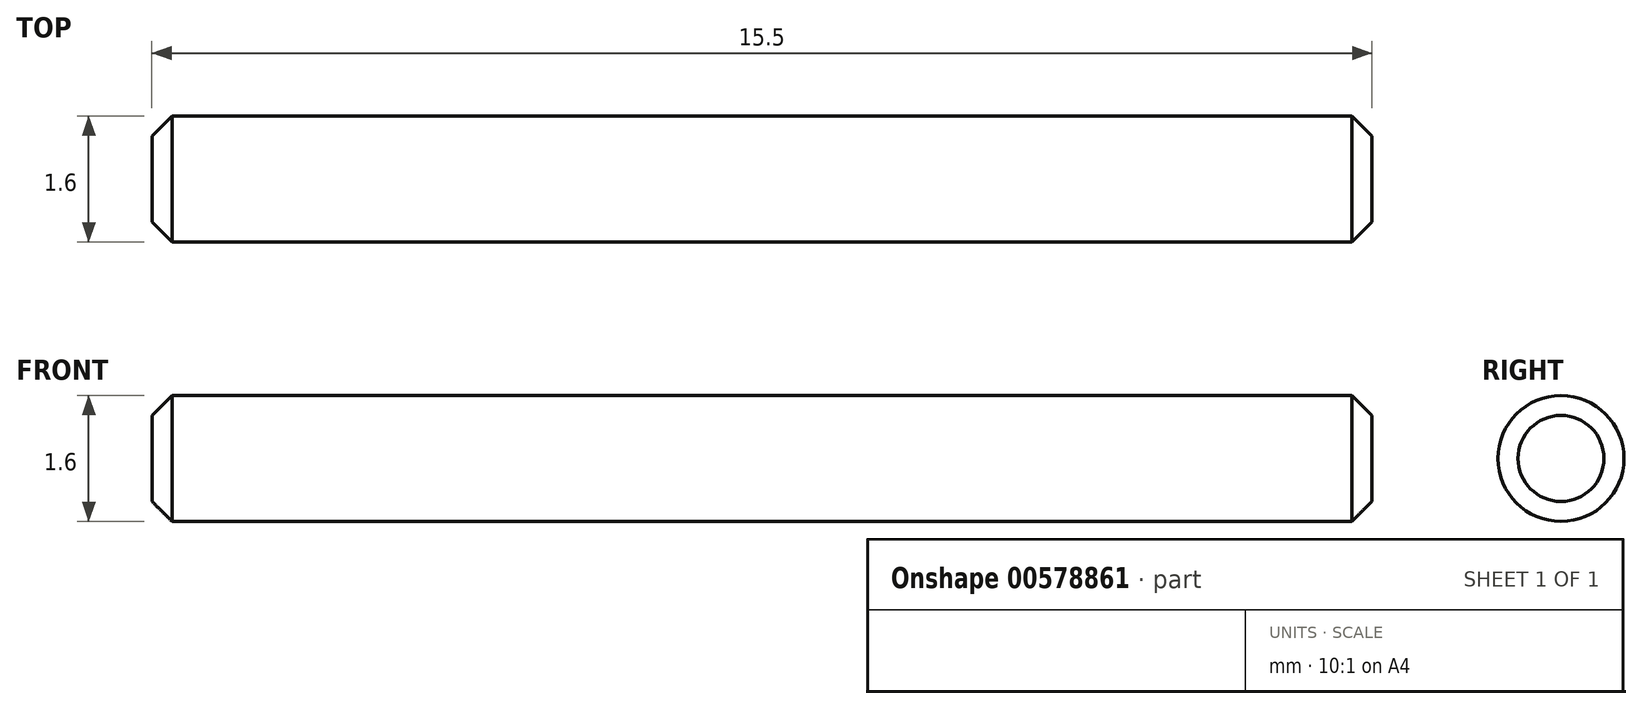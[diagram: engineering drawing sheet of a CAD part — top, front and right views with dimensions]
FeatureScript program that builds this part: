
annotation { "Feature Type Name" : "Feature", "Feature Type Description" : "" }
export const myFeature = defineFeature(function(context is Context, id is Id, definition is map)
    precondition{}
    {
        {
            var Q0;
            Q0=qCreatedBy(makeId("Right.planeOp"),FACE);
            var sketch = newSketch(context, id + "F0", { "sketchPlane" : qUnion([Q0])});
            skCircle(sketch, "E0", {"center": v(0, 0) * mm, "radius": 0.8 * mm});
            skSolve(sketch);
        }
        {
            var Q0;
            Q0=qSketchRegion(id+"F0",true);
            extrude(context, id + "F1", {"entities" : qUnion([Q0]), "endBound" : BoundingType.SYMMETRIC, "depth" : 15.5 * mm});
        }
        {
            var Q0;
            Q0=makeQuery(id+"F1.opExtrude","CAP_EDGE",EDGE,{"disambiguationData":[OSD([sQuery(id+"F0.wireOp",EDGE,"E0")])],"isStart":true});
            var Q1;
            Q1=makeQuery(id+"F1.opExtrude","CAP_EDGE",EDGE,{"disambiguationData":[OSD([sQuery(id+"F0.wireOp",EDGE,"E0")])],"isStart":false});
            chamfer(context, id + "F2", {"entities" : qUnion([Q0, Q1]), "width" : 0.25 * mm, "tangentPropagation" : true});
        }
    });
